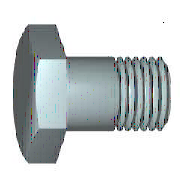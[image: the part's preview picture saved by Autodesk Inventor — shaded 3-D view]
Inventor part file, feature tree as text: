
AUTODESK INVENTOR PART (.ipt)
format: ipt  version: 2021 (Build 250183000, 183)  size: 194,560 bytes
history: native  units: mm (DEFAULTED — no unit token found)
features: sketch x3, extrude x1, chamfer x1, plane x1
ambient origin geometry x7: Origin, YZ Plane, XZ Plane, X Axis, Y Axis, Z Axis, Center Point
bodies: Solid1 (feature_tree), Body (feature_tree)
feature tree (6):
  extrude  "Head"  Depth=22.9mm
  chamfer  "Chamfer1"  Distance=2.4mm
  plane  "Work Plane1"
  sketch  "Sketch1"  dims[d0=25.0mm d1=22.9mm]
  sketch  "Sketch2"  dims[d2=4.0mm]
  sketch  "Sketch4"  dims[d12=90.0deg d3=2.4mm d4=0.0mm d5=30.0deg d21=90.0deg d6=0.429415mm d7=0.429515mm d8=0.0mm d9=0.4001mm d10=7.0mm d11=7.0mm d13=0.429515mm d14=4.0mm d15=22.9mm d16=0.0mm d19=7.0mm d55=45.0deg d57=0.0mm d58=0.0mm]
